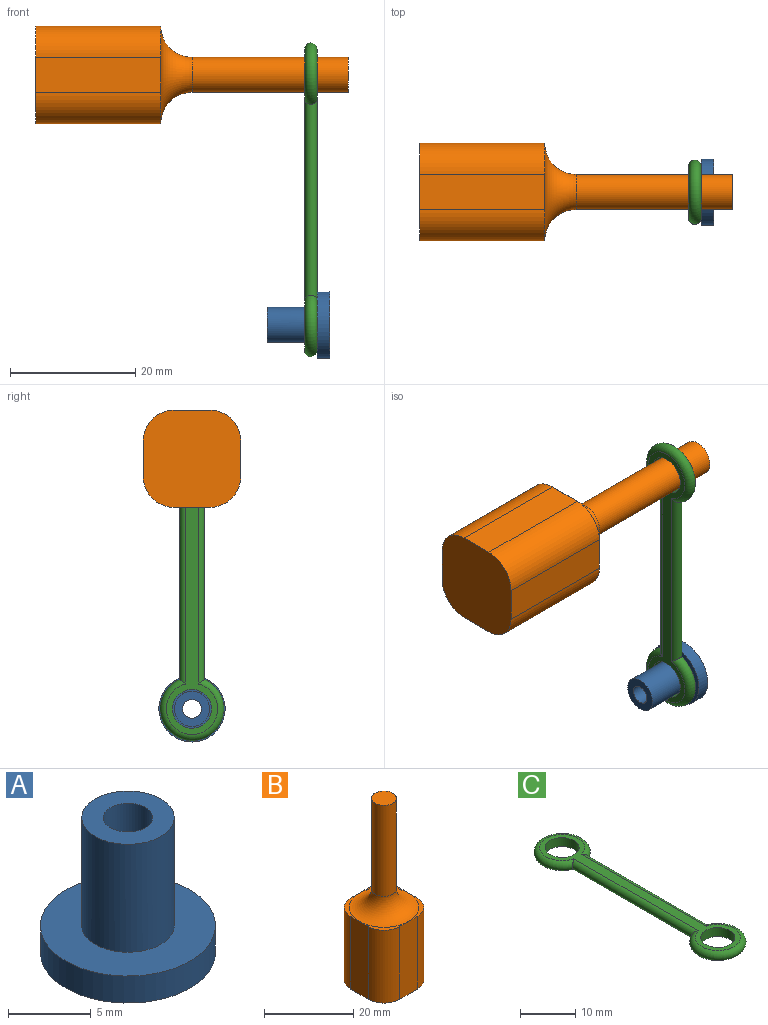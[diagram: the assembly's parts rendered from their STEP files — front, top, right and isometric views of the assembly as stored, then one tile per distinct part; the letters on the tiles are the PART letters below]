
ASSEMBLY  parts=3 mates=2
PART A: 6 faces, bbox 10.6x10.6x10 mm
  f0: cylinder r=2.8mm len=8mm, axis (0,0,-1), area 140.7mm2, adj f2,f5
  f1: cylinder r=1.5mm len=10mm, axis (0,0,-1), area 94.2mm2, adj f2,f3
  f2: plane 5.6x5.6mm, normal (0,0,1), area 17.6mm2, adj f0,f1
  f3: plane 10.6x10.6mm, normal (0,0,-1), area 81.2mm2, adj f1,f4
  f4: cylinder r=5.3mm len=10.6mm, axis (0,0,-1), area 66.6mm2, adj f3,f5
  f5: plane 10.6x10.6mm, normal (0,0,1), area 63.6mm2, adj f0,f4
PART B: 16 faces, bbox 24.6x24.6x50 mm
  f0: plane 7.8x7.8mm, normal (0,0,1), area 7.7mm2, adj f7,f8,f11,f14
  f1: plane 7.8x7.8mm, normal (0,0,1), area 7.7mm2, adj f6,f7,f11,f13
  f2: plane 7.8x7.8mm, normal (0,0,1), area 7.7mm2, adj f5,f6,f11,f12
  f3: cylinder r=2.8mm len=25mm, axis (0,0,-1), area 439.8mm2, adj f4,f11
  f4: plane 5.6x5.6mm, normal (0,0,1), area 24.6mm2, adj f3
  f5: plane 20x5.6mm, normal (0,1,0), area 112mm2, adj f2,f9,f10,f12,f15
  f6: plane 20x5.6mm, normal (-1,0,0), area 112mm2, adj f1,f2,f9,f12,f13
  f7: plane 20x5.6mm, normal (0,-1,0), area 112mm2, adj f0,f1,f9,f13,f14
  f8: plane 20x5.6mm, normal (1,0,0), area 112mm2, adj f0,f9,f10,f14,f15
  f9: plane 15.6x15.6mm, normal (0,0,-1), area 221.9mm2, adj f5,f6,f7,f8,f12,f13,f14,f15
  f10: plane 7.8x7.8mm, normal (0,0,1), area 7.7mm2, adj f5,f8,f11,f15
  f11: torus R=7.8mm, axis (0,0,1), area 227.8mm2, adj f0,f1,f2,f3,f10
  f12: cylinder r=5mm len=20mm, axis (0,0,-1), area 157.1mm2, adj f2,f5,f6,f9
  f13: cylinder r=5mm len=20mm, axis (0,0,1), area 157.1mm2, adj f1,f6,f7,f9
  f14: cylinder r=5mm len=20mm, axis (0,0,-1), area 157.1mm2, adj f0,f7,f8,f9
  f15: cylinder r=5mm len=20mm, axis (0,0,1), area 157.1mm2, adj f5,f8,f9,f10
PART C: 8 faces, bbox 11x51x2 mm
  f0: cylinder r=3.1mm len=6.2mm, axis (0,0,-1), area 39mm2, adj f2,f3
  f1: cylinder r=3.1mm len=6.2mm, axis (0,0,-1), area 39mm2, adj f2,f3
  f2: plane 48.2x8.2mm, normal (0,0,1), area 109mm2, adj f0,f1,f4,f5,f6,f7
  f3: plane 48.2x8.2mm, normal (0,0,-1), area 109mm2, adj f0,f1,f4,f5,f6,f7
  f4: cylinder r=1mm len=32.05mm, axis (0,1,0), area 97.8mm2, adj f2,f3,f5,f6
  f5: torus R=4.1mm, axis (0,0,1), area 83mm2, adj f2,f3,f4,f7
  f6: torus R=4.1mm, axis (0,0,1), area 83mm2, adj f2,f3,f4,f7
  f7: cylinder r=1mm len=32.05mm, axis (0,-1,0), area 97.8mm2, adj f2,f3,f5,f6
PLACE A rot(axis=(0,-1,0),90deg) t=(-5.56,-9.06,-29.9)mm
PLACE B rot(axis=(0,1,0),90deg) t=(-32.56,-9.06,10.1)mm
PLACE C rot(axis=(-0.58,0.58,-0.58),120deg) t=(-9.56,-9.06,-9.9)mm
MATE fastened C.f0 <-> B.f3  axis (1,0,0) through (-7.56,-9.06,10.1)mm
MATE fastened A.f4 <-> C.f5  axis (-1,0,0) through (-7.56,-9.06,-29.9)mm
